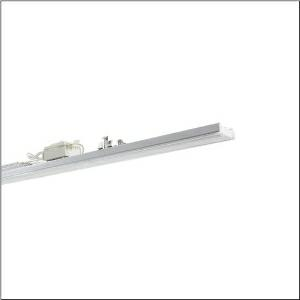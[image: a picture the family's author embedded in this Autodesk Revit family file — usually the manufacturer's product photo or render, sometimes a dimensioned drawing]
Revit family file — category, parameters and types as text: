
# Revit family: licross_11_recessed_extreme_mo_51te12dv4fxge
name_source: partatom
category: Lighting Fixtures
units: mm (PartAtom-declared; Revit-internal decimal feet)

## family parameters
Cut with Voids When Loaded = No
Host = Face
Light Source = No
Part Type = Normal
Room Calculation Point = No
Round Connector Dimension = Use Diameter
Shared = No

## types (1)
- --- (1 x LED, 15360 lm, 84.1 W, 4000K)
    Apparent Load = 84 VA
    CIE Flux Codes = 67 92 99 100 100
    Color Rendering = 80
    Color Temperature = 4000K
    Default Elevation = 1800 mm
    Description = Licross 11 Recessed extreme MO, luminaire insert, of sheet steel, galvanised, coil coated, white, length: 2.250mm, width: 66mm, height: 67mm, LED rated luminous flux: 15.360lm, light colour: 840, SDCM (Standard Deviation of Colour Matching)MacAdam ≤ 2 SDCM (initial), control gear: DALI 2, with plug, 5-pole, with phase selection, mains connection: 220..240V, AC, 50/60Hz, rated input power: 84W, internal wiring halogen-free, primary optical cover: cover, of PMMA, light emission: direct distribution, primary light characteristic: symmetric, protection rating (complete): IP54, insulation class (complete): insulation class I (protective earthing), certification: CE, ENEC, VDE, UKCA, protection symbol: D if used in an environment with non-conductive dust loads with corresponding accessories, impact resistance: IK06, permissible ambient temperature for indoor applications: -40..+45°C, corresponds to IFS (International Featured Standards) requirements for safety and quality in the food industry, reducing of maximum allowable ambient temperature of 5°C with ceiling mounting, LABS conformity tested according to VDMA 24364:2018-05, The light source and the operating device comply with the requirements of the Ecodesign Regulation (EU) 2019/2020 and are replaceable in accordance with this regulation, packaging unit: 1 piece
    Height = 58 mm
    Lamp = 1 x LED
    Lamp Light Flux = 15360 lm
    Lamp Power = 84.1 W
    Lamp count = 1
    Length = 2250 mm
    Luminous efficacy = 183 lm/W
    Manufacturer = Siteco
    ModVariant = No
    Model = 51TE12DV4FXGE
    Mounting Place = Ceiling
    Mounting Type = Pendant
    Number of Poles = 1
    OnlyDefault = Yes
    Power Factor = 1
    Product Name = Licross 11 Recessed extreme MO
    Product group = luminaire insert | ceiling pendant
    ProductGroupID = 901
    Protection Class = Protection class I
    Protection Degree = IP 54
    RLX_Detail_Level = 1
    RLX_Emergency_Light_Flux = 0 lm
    RLX_Emergency_Type = 0
    RLX_Emergency_Type_DB = No
    RlxData = <blob elided: 29525 chars, md5=eea2ba9a>
    Socket = socket
    Standby Power = 0 W
    System Light Flux = 15360 lm
    System Power = 84 W
    Type Comments = factory setting: luminous flux: 100 % | dim-lin: 254 | 378 mA
    Type Image = l_1296930.jpg
    URL = http://relux.com
    VarID = @adj_087491
    Voltage = 0 V
    Weight = 0.00 kg
    Width = 66 mm

## geometry (parser evidence)
native form markers: Blend x4, Sweep x11
no freeform markers — native parametric forms only
